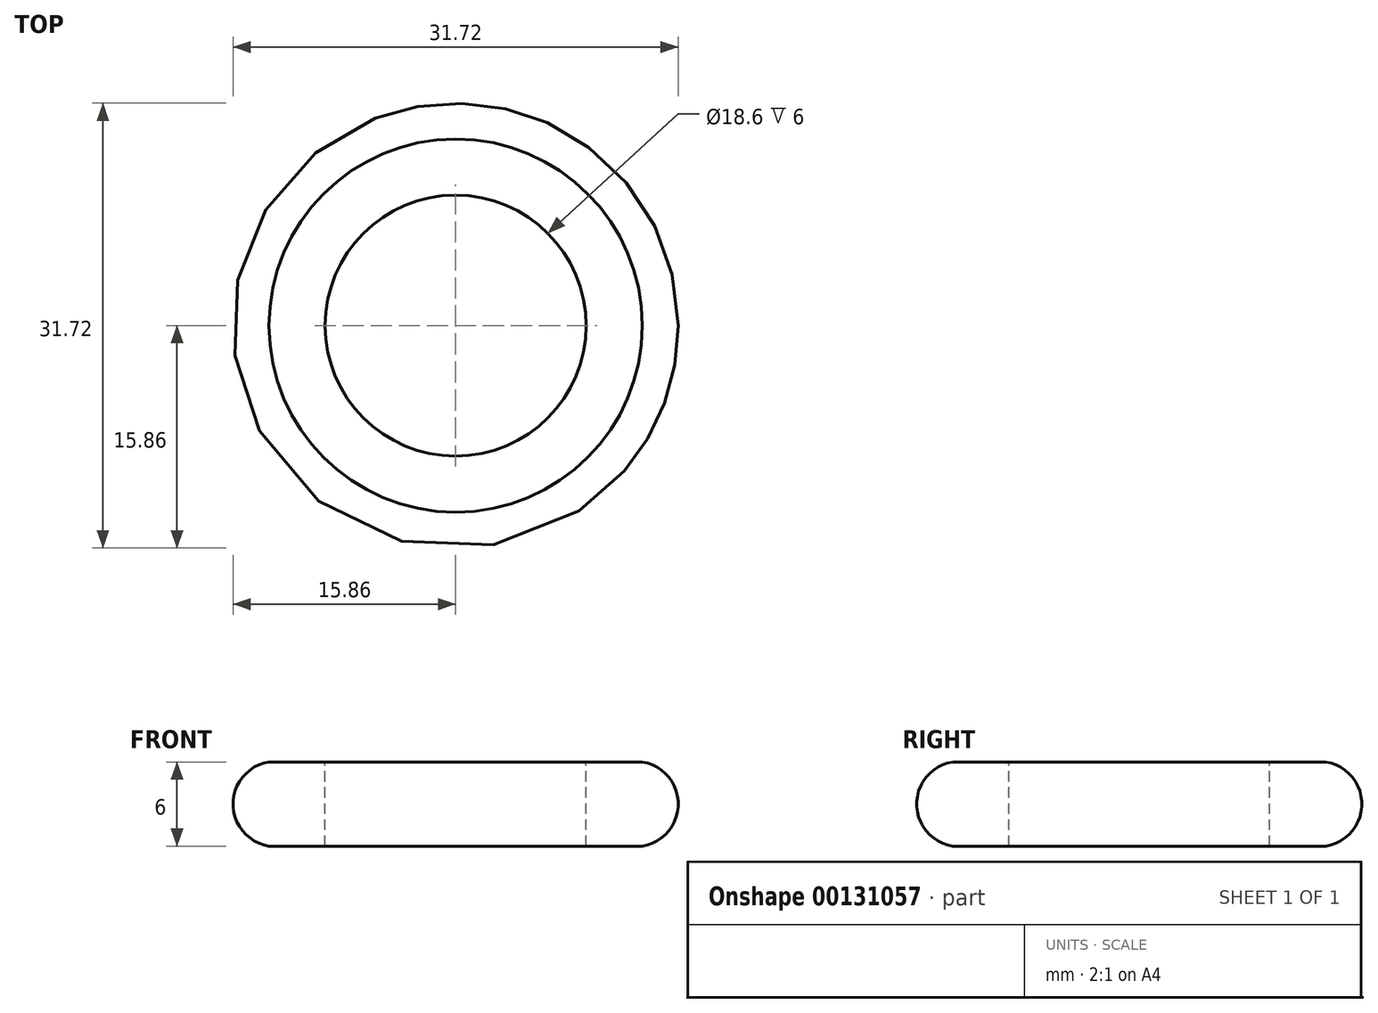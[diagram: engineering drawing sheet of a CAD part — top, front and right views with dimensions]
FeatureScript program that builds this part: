
annotation { "Feature Type Name" : "Feature", "Feature Type Description" : "" }
export const myFeature = defineFeature(function(context is Context, id is Id, definition is map)
    precondition{}
    {
        {
            var Q0;
            Q0=qCreatedBy(makeId("Right.planeOp"),FACE);
            var sketch = newSketch(context, id + "F0", { "sketchPlane" : qUnion([Q0])});
            skLineSegment(sketch, "E0.bottom", {"start": v(9.3, 3) * mm, "end": v(-9.3, 3) * mm});
            skLineSegment(sketch, "E0.top", {"start": v(9.3, -3) * mm, "end": v(-9.3, -3) * mm});
            skLineSegment(sketch, "E0.left", {"start": v(9.3, 3) * mm, "end": v(9.3, -3) * mm});
            skLineSegment(sketch, "E0.right", {"start": v(-9.3, 3) * mm, "end": v(-9.3, -3) * mm});
            skPoint(sketch, "E0.middle", {"position": v(0, 0) * mm});
            skLineSegment(sketch, "E1.bottom", {"start": v(-9.3, 3) * mm, "end": v(-13.3, 3) * mm});
            skLineSegment(sketch, "E1.top", {"start": v(-9.3, -3) * mm, "end": v(-13.3, -3) * mm});
            skLineSegment(sketch, "E1.right", {"start": v(-13.3, 3) * mm, "end": v(-13.3, -3) * mm});
            skArc(sketch, "E2", {"start": v(-13.3, 3) * mm, "mid": v(-15.86, 0) * mm, "end": v(-13.3, -3) * mm});
            skLineSegment(sketch, "E3", {"start": v(0, 3) * mm, "end": v(0, -3) * mm, "construction": true});
            skSolve(sketch);
        }
        {
            var Q0;
            Q0=makeQuery(id+"F0.imprint","IMPRINT",FACE,{"disambiguationData":[TD([[makeQuery(id+"F0.imprint","IMPRINT",EDGE,{"derivedFrom":sQuery(id+"F0.wireOp",EDGE,"E1.bottom")}),1.0]])]});
            var Q1;
            Q1=makeQuery(id+"F0.imprint","IMPRINT",FACE,{"disambiguationData":[TD([[makeQuery(id+"F0.imprint","IMPRINT",EDGE,{"derivedFrom":sQuery(id+"F0.wireOp",EDGE,"E1.right")}),-1.0]])]});
            var Q2;
            Q2=sQuery(id+"F0.wireOp",EDGE,"E3");
            revolve(context, id + "F1", {"surfaceOperationType" : NewSurfaceOperationType.NEW, "entities" : qUnion([Q0, Q1]), "axis" : qUnion([Q2]), "revolveType" : RevolveType.FULL});
        }
    });
